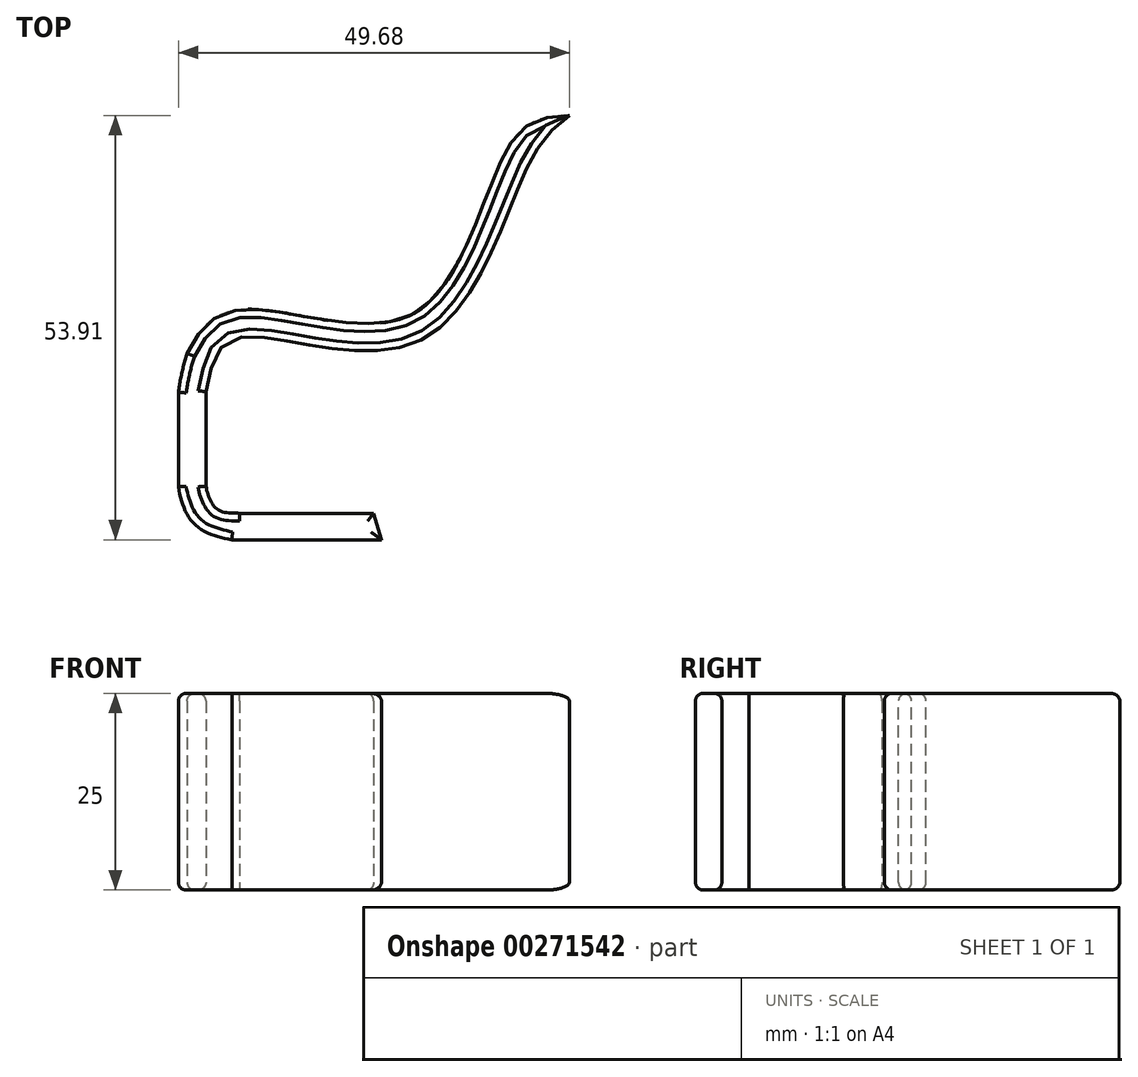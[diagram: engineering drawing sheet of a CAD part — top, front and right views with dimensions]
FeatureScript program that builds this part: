
annotation { "Feature Type Name" : "Feature", "Feature Type Description" : "" }
export const myFeature = defineFeature(function(context is Context, id is Id, definition is map)
    precondition{}
    {
        {
            var Q0;
            Q0=qCreatedBy(makeId("Top.planeOp"),FACE);
            var sketch = newSketch(context, id + "F0", { "sketchPlane" : qUnion([Q0])});
            skFitSpline(sketch, "E0", {"points": [v(29.67, 41) * mm, v(22.72, 38.21) * mm, v(9.98, 15.9) * mm, v(-12.74, 16.26) * mm, v(-19.99, 8.35) * mm], "startDerivative": vector(-44.26, -2.03) * mm, "endDerivative": vector(-23.33, -55.92) * mm});
            skFitSpline(sketch, "E1", {"points": [v(-16.5, 5.9) * mm, v(-15.52, 9.9) * mm, v(-12.05, 12.83) * mm, v(10.7, 12.4) * mm, v(24.78, 35.39) * mm, v(29.67, 41) * mm], "startDerivative": vector(7.73, 36.04) * mm, "endDerivative": vector(28.28, 21.43) * mm});
            skFitSpline(sketch, "E2", {"points": [v(-18.9, 10.77) * mm, v(-19.56, 8.35) * mm, v(-20, 5.81) * mm], "startDerivative": vector(-2, -6.25) * mm, "endDerivative": vector(-0.7, -5.96) * mm});
            skLineSegment(sketch, "E3", {"start": v(-20, 5.81) * mm, "end": v(-20, -4.19) * mm});
            skLineSegment(sketch, "E4", {"start": v(-16.5, 5.9) * mm, "end": v(-16.5, -6.1) * mm});
            skLineSegment(sketch, "E5", {"start": v(-20, -4.19) * mm, "end": v(-20, -6.19) * mm});
            skFitSpline(sketch, "E6", {"points": [v(-20, -6.19) * mm, v(-17.92, -10.96) * mm, v(-13.22, -12.9) * mm], "startDerivative": vector(1.68, -10.94) * mm, "endDerivative": vector(11.35, -2.24) * mm});
            skFitSpline(sketch, "E7", {"points": [v(-16.5, -6.1) * mm, v(-14.95, -9.1) * mm, v(-12.22, -9.55) * mm], "startDerivative": vector(1.4, -8.08) * mm, "endDerivative": vector(7.65, -0.59) * mm});
            skLineSegment(sketch, "E8", {"start": v(-13.22, -12.9) * mm, "end": v(5.78, -12.9) * mm});
            skLineSegment(sketch, "E9", {"start": v(-12.22, -9.55) * mm, "end": v(4.78, -9.55) * mm});
            skLineSegment(sketch, "E10", {"start": v(5.78, -12.9) * mm, "end": v(4.78, -9.55) * mm});
            skLineSegment(sketch, "E11", {"start": v(-13.86, 12.18) * mm, "end": v(-16.88, 13.94) * mm, "construction": true});
            skLineSegment(sketch, "E12", {"start": v(-12.97, 12.61) * mm, "end": v(-13.7, 16.04) * mm, "construction": true});
            skLineSegment(sketch, "E13", {"start": v(-5.24, 12.17) * mm, "end": v(-4.13, 15.48) * mm, "construction": true});
            skLineSegment(sketch, "E14", {"start": v(19.07, 30.56) * mm, "end": v(21.73, 28.28) * mm, "construction": true});
            skSolve(sketch);
        }
        {
            var Q0;
            Q0=makeQuery(id+"F0.imprint","IMPRINT",FACE,{"disambiguationData":[TD([[makeQuery(id+"F0.imprint","IMPRINT",EDGE,{"derivedFrom":sQuery(id+"F0.wireOp",EDGE,"E0")}),1.0]])]});
            extrude(context, id + "F1", {"entities" : qUnion([Q0]), "depth" : 25 * mm, "offsetDistance" : 25 * mm});
        }
        {
            var Q0;
            Q0=makeQuery(id+"F1.opExtrude","CAP_FACE",FACE,{"disambiguationData":[OSD([sQuery(id+"F0.wireOp",EDGE,"E0"),sQuery(id+"F0.wireOp",EDGE,"E1"),sQuery(id+"F0.wireOp",EDGE,"E2"),sQuery(id+"F0.wireOp",EDGE,"E3"),sQuery(id+"F0.wireOp",EDGE,"E4"),sQuery(id+"F0.wireOp",EDGE,"E5"),sQuery(id+"F0.wireOp",EDGE,"E6"),sQuery(id+"F0.wireOp",EDGE,"E7"),sQuery(id+"F0.wireOp",EDGE,"E8"),sQuery(id+"F0.wireOp",EDGE,"E9"),sQuery(id+"F0.wireOp",EDGE,"E10")])],"isStart":true});
            var Q1;
            Q1=makeQuery(id+"F1.opExtrude","CAP_FACE",FACE,{"disambiguationData":[OSD([sQuery(id+"F0.wireOp",EDGE,"E0"),sQuery(id+"F0.wireOp",EDGE,"E1"),sQuery(id+"F0.wireOp",EDGE,"E2"),sQuery(id+"F0.wireOp",EDGE,"E3"),sQuery(id+"F0.wireOp",EDGE,"E4"),sQuery(id+"F0.wireOp",EDGE,"E5"),sQuery(id+"F0.wireOp",EDGE,"E6"),sQuery(id+"F0.wireOp",EDGE,"E7"),sQuery(id+"F0.wireOp",EDGE,"E8"),sQuery(id+"F0.wireOp",EDGE,"E9"),sQuery(id+"F0.wireOp",EDGE,"E10")])],"isStart":false});
            fillet(context, id + "F2", {"entities" : qUnion([Q0, Q1]), "radius" : 1 * mm, "tangentPropagation" : true, "allowEdgeOverflow" : false});
        }
    });
